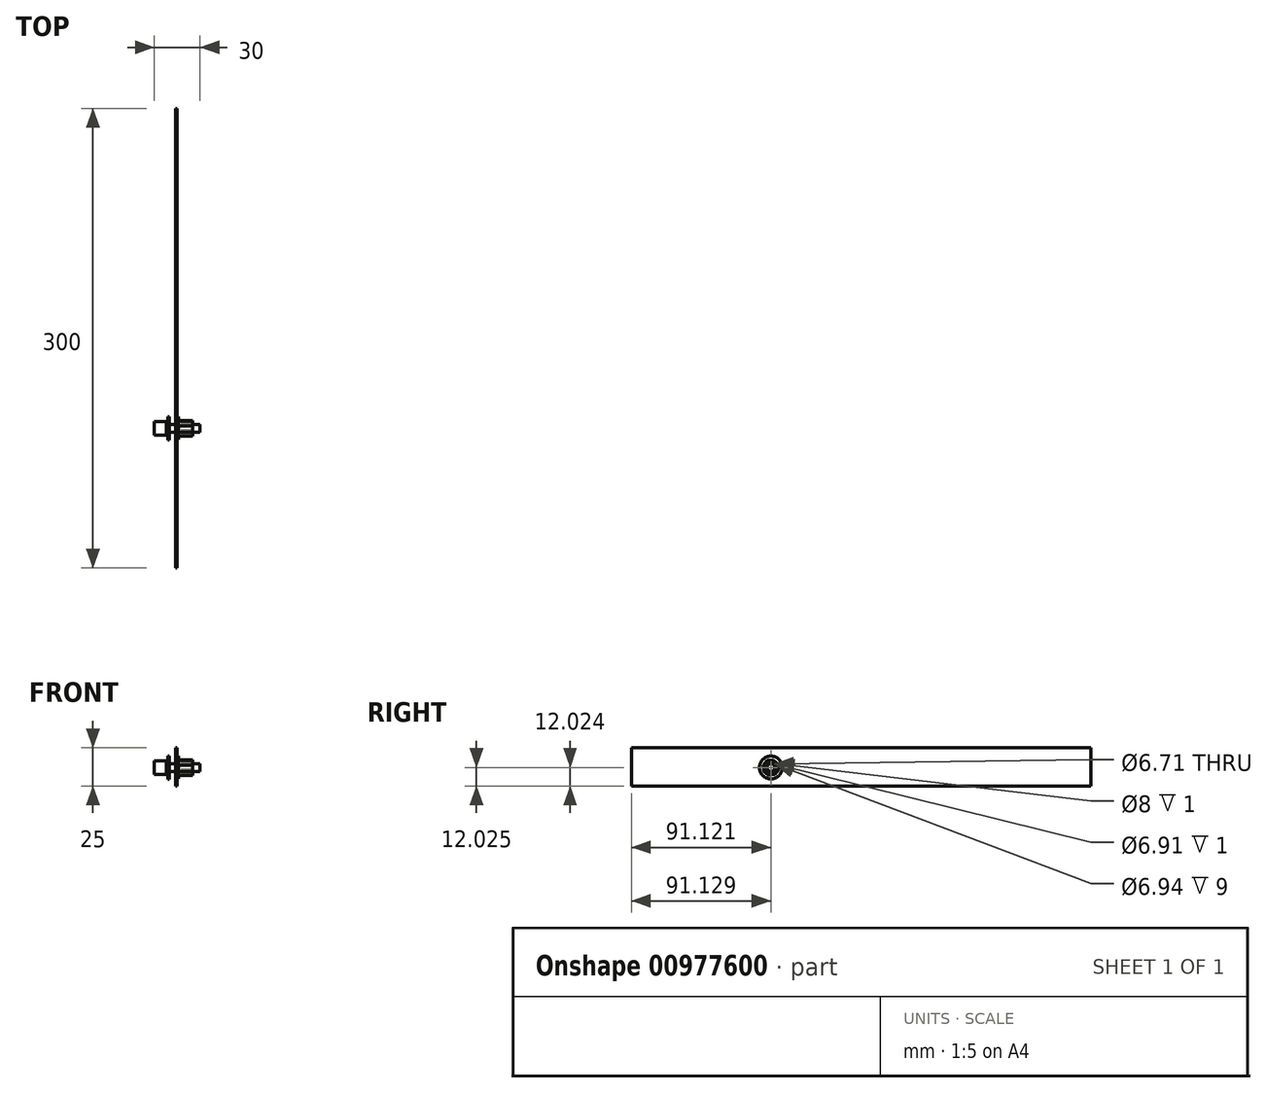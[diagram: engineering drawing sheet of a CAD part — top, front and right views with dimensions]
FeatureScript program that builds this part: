
annotation { "Feature Type Name" : "Feature", "Feature Type Description" : "" }
export const myFeature = defineFeature(function(context is Context, id is Id, definition is map)
    precondition{}
    {
        {
            var Q0;
            Q0=qCreatedBy(makeId("Top.planeOp"),FACE);
            var sketch = newSketch(context, id + "F0", { "sketchPlane" : qUnion([Q0])});
            skLineSegment(sketch, "E0.bottom", {"start": v(0, 0) * mm, "end": v(1, 0) * mm});
            skLineSegment(sketch, "E0.top", {"start": v(0, -300) * mm, "end": v(1, -300) * mm});
            skLineSegment(sketch, "E0.left", {"start": v(0, 0) * mm, "end": v(0, -300) * mm});
            skLineSegment(sketch, "E0.right", {"start": v(1, 0) * mm, "end": v(1, -300) * mm});
            skSolve(sketch);
        }
        {
            var Q0;
            Q0=makeQuery(id+"F0.imprint","IMPRINT",FACE,{"disambiguationData":[TD([[makeQuery(id+"F0.imprint","IMPRINT",EDGE,{"derivedFrom":sQuery(id+"F0.wireOp",EDGE,"E0.bottom")}),-1.0]])]});
            extrude(context, id + "F1", {"entities" : qUnion([Q0]), "depth" : 25 * mm, "offsetDistance" : 25 * mm});
        }
        {
            var Q0;
            Q0=makeQuery(id+"F1.opExtrude","SWEPT_FACE",FACE,{"disambiguationData":[OSD([sQuery(id+"F0.wireOp",EDGE,"E0.right")])]});
            var sketch = newSketch(context, id + "F2", { "sketchPlane" : qUnion([Q0])});
            skCircle(sketch, "E1", {"center": v(-208.88, 12.03) * mm, "radius": 4 * mm});
            skSolve(sketch);
        }
        {
            var Q0;
            Q0=sQuery(id+"F2.wireOp",VERTEX,"E1.center");
            var Q1;
            Q1=makeQuery(id+"F1.opExtrude","SWEPT_BODY",BODY,{"disambiguationData":[OSD([sQuery(id+"F0.wireOp",EDGE,"E0.bottom"),sQuery(id+"F0.wireOp",EDGE,"E0.top"),sQuery(id+"F0.wireOp",EDGE,"E0.left"),sQuery(id+"F0.wireOp",EDGE,"E0.right")])]});
            hole(context, id + "F3", {"style" : HoleStyle.SIMPLE, "endStyle" : HoleEndStyle.THROUGH, "holeDiameter" : 8 * mm, "majorDiameter" : 5 * mm, "isTappedThrough" : true, "tappedDepth" : 12 * mm, "tapClearance" : 3, "locations" : qUnion([Q0]), "scope" : qUnion([Q1])});
        }
        {
            var Q0;
            Q0=makeQuery(id+"F1.opExtrude","SWEPT_FACE",FACE,{"disambiguationData":[OSD([sQuery(id+"F0.wireOp",EDGE,"E0.right")])]});
            var sketch = newSketch(context, id + "F4", { "sketchPlane" : qUnion([Q0])});
            skCircle(sketch, "E2", {"center": v(-208.87, 12.02) * mm, "radius": 2.5 * mm});
            skSolve(sketch);
        }
        {
            var Q0;
            Q0=makeQuery(id+"F4.imprint","IMPRINT",FACE,{"disambiguationData":[TD([[makeQuery(id+"F4.imprint","IMPRINT",EDGE,{"derivedFrom":sQuery(id+"F4.wireOp",EDGE,"E2")}),1.0]])]});
            extrude(context, id + "F5", {"entities" : qUnion([Q0]), "depth" : 15 * mm, "offsetDistance" : 25 * mm});
        }
        {
            var Q0;
            Q0=makeQuery(id+"F5.opExtrude","CAP_FACE",FACE,{"disambiguationData":[OSD([sQuery(id+"F4.wireOp",EDGE,"E2")])],"isStart":true});
            extrude(context, id + "F6", {"entities" : qUnion([Q0]), "operationType" : NewBodyOperationType.ADD, "depth" : 5 * mm, "offsetDistance" : 25 * mm});
        }
        {
            var Q0;
            Q0=makeQuery(id+"F6.opExtrude","CAP_FACE",FACE,{"disambiguationData":[OSD([sQuery(id+"F4.wireOp",EDGE,"E2")])],"isStart":false});
            var sketch = newSketch(context, id + "F7", { "sketchPlane" : qUnion([Q0])});
            skCircle(sketch, "E3", {"center": v(208.87, 12.02) * mm, "radius": 7.62 * mm});
            skCircle(sketch, "E4", {"center": v(208.87, 12.02) * mm, "radius": 3.35 * mm});
            skSolve(sketch);
        }
        {
            var Q0;
            Q0=makeQuery(id+"F7.imprint","IMPRINT",FACE,{"disambiguationData":[TD([[makeQuery(id+"F7.imprint","IMPRINT",EDGE,{"derivedFrom":sQuery(id+"F7.wireOp",EDGE,"E3")}),1.0]])]});
            extrude(context, id + "F8", {"entities" : qUnion([Q0]), "depth" : 1 * mm, "offsetDistance" : 25 * mm});
        }
        {
            var Q0;
            Q0=makeQuery(id+"F6.opExtrude","CAP_FACE",FACE,{"disambiguationData":[OSD([sQuery(id+"F4.wireOp",EDGE,"E2")])],"isStart":false});
            extrude(context, id + "F9", {"entities" : qUnion([Q0]), "operationType" : NewBodyOperationType.ADD, "depth" : 2 * mm, "offsetDistance" : 25 * mm});
        }
        {
            var Q0;
            Q0=makeQuery(id+"F9.opExtrude","CAP_FACE",FACE,{"disambiguationData":[OSD([sQuery(id+"F4.wireOp",EDGE,"E2")])],"isStart":false});
            var sketch = newSketch(context, id + "F10", { "sketchPlane" : qUnion([Q0])});
            skCircle(sketch, "E5", {"center": v(208.87, 12.02) * mm, "radius": 4.47 * mm});
            skSolve(sketch);
        }
        {
            var Q0;
            Q0 = qSketchRegion(id + "F10", true);
            extrude(context, id + "F11", {"entities" : qUnion([Q0]), "depth" : 8 * mm, "offsetDistance" : 25 * mm});
        }
        {
            var Q0;
            Q0=makeQuery(id+"F1.opExtrude","SWEPT_FACE",FACE,{"disambiguationData":[OSD([sQuery(id+"F0.wireOp",EDGE,"E0.right")])]});
            var sketch = newSketch(context, id + "F12", { "sketchPlane" : qUnion([Q0])});
            skCircle(sketch, "E6", {"center": v(-208.88, 12.03) * mm, "radius": 7.47 * mm});
            skCircle(sketch, "E7", {"center": v(-208.88, 12.03) * mm, "radius": 3.46 * mm});
            skSolve(sketch);
        }
        {
            var Q0;
            Q0 = qSketchRegion(id + "F12", true);
            extrude(context, id + "F13", {"entities" : qUnion([Q0]), "operationType" : NewBodyOperationType.ADD, "depth" : 1 * mm, "offsetDistance" : 25 * mm});
        }
        {
            var Q0;
            Q0=makeQuery(id+"F13.opExtrude","CAP_FACE",FACE,{"disambiguationData":[OSD([sQuery(id+"F12.wireOp",EDGE,"E6"),sQuery(id+"F12.wireOp",EDGE,"E7")])],"isStart":false});
            var sketch = newSketch(context, id + "F14", { "sketchPlane" : qUnion([Q0])});
            skLineSegment(sketch, "E8.0", {"start": v(-207.43, 17.07) * mm, "end": v(-204.29, 14.57) * mm});
            skLineSegment(sketch, "E8.1", {"start": v(-204.29, 14.57) * mm, "end": v(-203.83, 10.58) * mm});
            skLineSegment(sketch, "E8.2", {"start": v(-203.83, 10.58) * mm, "end": v(-206.33, 7.43) * mm});
            skLineSegment(sketch, "E8.3", {"start": v(-206.33, 7.43) * mm, "end": v(-210.33, 6.98) * mm});
            skLineSegment(sketch, "E8.4", {"start": v(-210.33, 6.98) * mm, "end": v(-213.47, 9.48) * mm});
            skLineSegment(sketch, "E8.5", {"start": v(-213.47, 9.48) * mm, "end": v(-213.93, 13.47) * mm});
            skLineSegment(sketch, "E8.6", {"start": v(-213.93, 13.47) * mm, "end": v(-211.42, 16.62) * mm});
            skLineSegment(sketch, "E8.7", {"start": v(-211.42, 16.62) * mm, "end": v(-207.43, 17.07) * mm});
            skCircle(sketch, "E9", {"center": v(-208.88, 12.03) * mm, "radius": 3.47 * mm});
            skSolve(sketch);
        }
        {
            var Q0;
            Q0 = qSketchRegion(id + "F14", true);
            extrude(context, id + "F15", {"entities" : qUnion([Q0]), "operationType" : NewBodyOperationType.ADD, "depth" : 9 * mm, "offsetDistance" : 25 * mm});
        }
    });
